# Revit family: BIM_RGV_INFINITY_F4_DN40_DN300_PN10_16_SQC
name_source: partatom
category: Pipe Accessories
revit_build: Autodesk Revit 2017 (Build: 20160225_1515(x64)
units: mm (PartAtom-declared; Revit-internal decimal feet)

## family parameters
Always vertical = Yes
Cut with Voids When Loaded = No
Part Type = Valve - Breaks Into
Round Connector Dimension = Use Diameter
Shared = No
Work Plane-Based = No

## types (10) — shared parameters
Acces Clearance Bottom = Maintenance free according to IOM-RGV17
Acces Clearance Front = Maintenance free according to IOM-RGV17
Acces Clearance Left = Maintenance free according to IOM-RGV17
Acces Clearance Rear = Maintenance free according to IOM-RGV17
Acces Clearance Right = Maintenance free according to IOM-RGV17
Acces Clearance Top = Maintenance free according to IOM-RGV17
Approval = WRAS
Body, Bonnet Seal Material = EN 681-1 EPDM
Bonnet Bolts Material = STEEL 12.9 (GEOMET)
By-Pass = No
CE Approval = CE-0056-PED-H-BEL 001-17-ESP
Coating = Fusion bonded epoxy, 250µm
Connection Type = Flange
Direction of Closure = Clockwise
Lower Limit Temperature, Deg C = -10 mm  [stored -0.0328084 ft]
Manufacturer = Belgicast International S.L.
Manufacturer website = http://www.belgicast.eu
Operating Element = Stem Cap
Packing Gland Material = Copper alloy BS EN 12165, CW617N
Pressure Rating = PN16
Seat Type = Resilient Seat
Stem Material = 431S29 acc. to BS-970
Test Pressure, Bar(g) = Body: 24bar / Seat: 17.6bar
Thrust Collar Material = NA. It is part of the stem in Infinity design
Upper Limit Operating Pressure, Bar(g) = 16 mm  [stored 0.0524934 ft]
Upper Limit Temperature, Deg C = 50 mm  [stored 0.164042 ft]
Wedge Assembly Material = Ductile iron, BS EN 1563 EN-GJS-500-7. Fully coated with EN 681-1 EPDM rubber WRAS listed, complete with wedge nut of copper alloy BS EN 12165, CW 307G

## per-type parameters (varying)
| type | Body Material | Bonnet Material | Connection Size | Features | Gross Weight | Nominal Diameter | Normal Operating Torque, N.m | Number of turns fully open to fully closed | PED Category | Product Model Number | Stem Cap Material | Upper Limit Torque at Max PN, N.m |
| DN80 | Ductile (SG) Iron, BSEN1563 EN-GJS-500-21 | Ductile (SG) Iron, BSEN1563 EN-GJS-500-21 | DN80 | INFTY.Z.BS "B" DN80 PN16 MIC. CUA. | 15.8kg | 80 mm  [stored 0.262467 ft] | 60 mm  [stored 0.19685 ft] | 7 mm  [stored 0.0229659 ft] | It does not apply, according to article 3, paragraph 17 | RGV00479TS | Ductile (SG) Iron, BSEN1563 EN-GJS-500-21 | 140 mm  [stored 0.459318 ft] |
| DN100 | Ductile (SG) Iron, BSEN1563 EN-GJS-500-28 | Ductile (SG) Iron, BSEN1563 EN-GJS-500-28 | DN100 | INFTY.Z.BS "B" DN100 PN16 MIC. CUA. | 18.2kg | 100 mm  [stored 0.328084 ft] | 70 mm  [stored 0.229659 ft] | 9 mm | It does not apply, according to article 3, paragraph 24 | RGV004DN80TS | Ductile (SG) Iron, BSEN1563 EN-GJS-500-28 | 160 mm  [stored 0.524934 ft] |
| DN65 | Ductile (SG) Iron, BSEN1563 EN-GJS-500-14 | Ductile (SG) Iron, BSEN1563 EN-GJS-500-14 | DN65 | INFTY.Z.BS "B" DN65 PN16 MIC. CUA. | 13.5kg | 65 mm  [stored 0.213255 ft] | 60 mm  [stored 0.19685 ft] | 6 mm  [stored 0.019685 ft] | It does not apply, according to article 3, paragraph 10 | RGV00478TS | Ductile (SG) Iron, BSEN1563 EN-GJS-500-14 | 125 mm  [stored 0.410105 ft] |
| DN50 | Ductile (SG) Iron, BSEN1563 EN-GJS-500-7 | Ductile (SG) Iron, BSEN1563 EN-GJS-500-7 | DN50 | INFTY.Z.BS "B" DN50 PN16 MIC. CUA. | 10kg | 50 mm  [stored 0.164042 ft] | 40 mm  [stored 0.131234 ft] | 5 mm  [stored 0.0164042 ft] | It does not apply, according to article 3, paragraph 3 | RGV00477TS | Ductile (SG) Iron, BSEN1563 EN-GJS-500-7 | 110 mm  [stored 0.360892 ft] |
| DN125 | Ductile (SG) Iron, BSEN1563 EN-GJS-500-35 | Ductile (SG) Iron, BSEN1563 EN-GJS-500-35 | DN125 | INFTY.Z.BS "B" DN125 PN16 MIC. CUA. | 24.6kg | 125 mm  [stored 0.410105 ft] | 100 mm  [stored 0.328084 ft] | 11 mm  [stored 0.0360892 ft] | It does not apply, according to article 3, paragraph 31 | RGV00481TS | Ductile (SG) Iron, BSEN1563 EN-GJS-500-35 | 185 mm  [stored 0.606955 ft] |
| DN150 | Ductile (SG) Iron, BSEN1563 EN-GJS-500-42 | Ductile (SG) Iron, BSEN1563 EN-GJS-500-42 | DN150 | INFTY.Z.BS "B" DN125 PN16 MIC. CUA. | 29.5kg | 150 mm  [stored 0.492126 ft] | 100 mm  [stored 0.328084 ft] | 130 mm  [stored 0.426509 ft] | It does not apply, according to article 3, paragraph 38 | RGV00482TS | Ductile (SG) Iron, BSEN1563 EN-GJS-500-42 | 210 mm  [stored 0.688976 ft] |
| DN200 | Ductile (SG) Iron, BSEN1563 EN-GJS-500-49 | Ductile (SG) Iron, BSEN1563 EN-GJS-500-49 | DN200 | INFTY.Z.BS "B" DN125 PN16 MIC. CUA. | 50.8kg | 200 mm  [stored 0.656168 ft] | 140 mm  [stored 0.459318 ft] | 17 mm | It does not apply, according to article 3, paragraph 45 | RGV00484TS | Ductile (SG) Iron, BSEN1563 EN-GJS-500-49 | 260 mm  [stored 0.853018 ft] |
| DN250 | Ductile (SG) Iron, BSEN1563 EN-GJS-500-61 | Ductile (SG) Iron, BSEN1563 EN-GJS-500-61 | DN250 | INFTY.Z.BS "B" DN125 PN16 MIC. CUA. | 73.9kg | 250 mm  [stored 0.82021 ft] | 200 mm  [stored 0.656168 ft] | 21 mm  [stored 0.0688976 ft] | It does not apply, according to article 3, paragraph 57 | RGV00486TS | Ductile (SG) Iron, BSEN1563 EN-GJS-500-61 | 310 mm  [stored 1.01706 ft] |
| DN300 | Ductile (SG) Iron, BSEN1563 EN-GJS-500-73 | Ductile (SG) Iron, BSEN1563 EN-GJS-500-73 | DN300 | INFTY.Z.BS"B"DN300PN16 MIC.CUA. | 99.9kg | 300 mm  [stored 0.984252 ft] | 220 mm  [stored 0.721785 ft] | 26 mm | It does not apply, according to article 3, paragraph 69 | RGV00488TS | Ductile (SG) Iron, BSEN1563 EN-GJS-500-73 | 360 mm  [stored 1.1811 ft] |
| DN40 | Ductile (SG) Iron, BSEN1563 EN-GJS-500-7 | Ductile (SG) Iron, BSEN1563 EN-GJS-500-7 | DN50 | INFTY.Z.BS "B" DN50 PN16 MIC. CUA. | 10kg | 40 mm  [stored 0.131234 ft] | 40 mm  [stored 0.131234 ft] | 5 mm  [stored 0.0164042 ft] | It does not apply, according to article 3, paragraph 3 | RGV00477TS | Ductile (SG) Iron, BSEN1563 EN-GJS-500-7 | 110 mm  [stored 0.360892 ft] |

note: [stored X ft] marks values corroborated as IEEE doubles in the binary element streams (Revit-internal decimal feet)

## geometry (parser evidence)
native form markers: Sweep x2
no freeform markers — native parametric forms only
